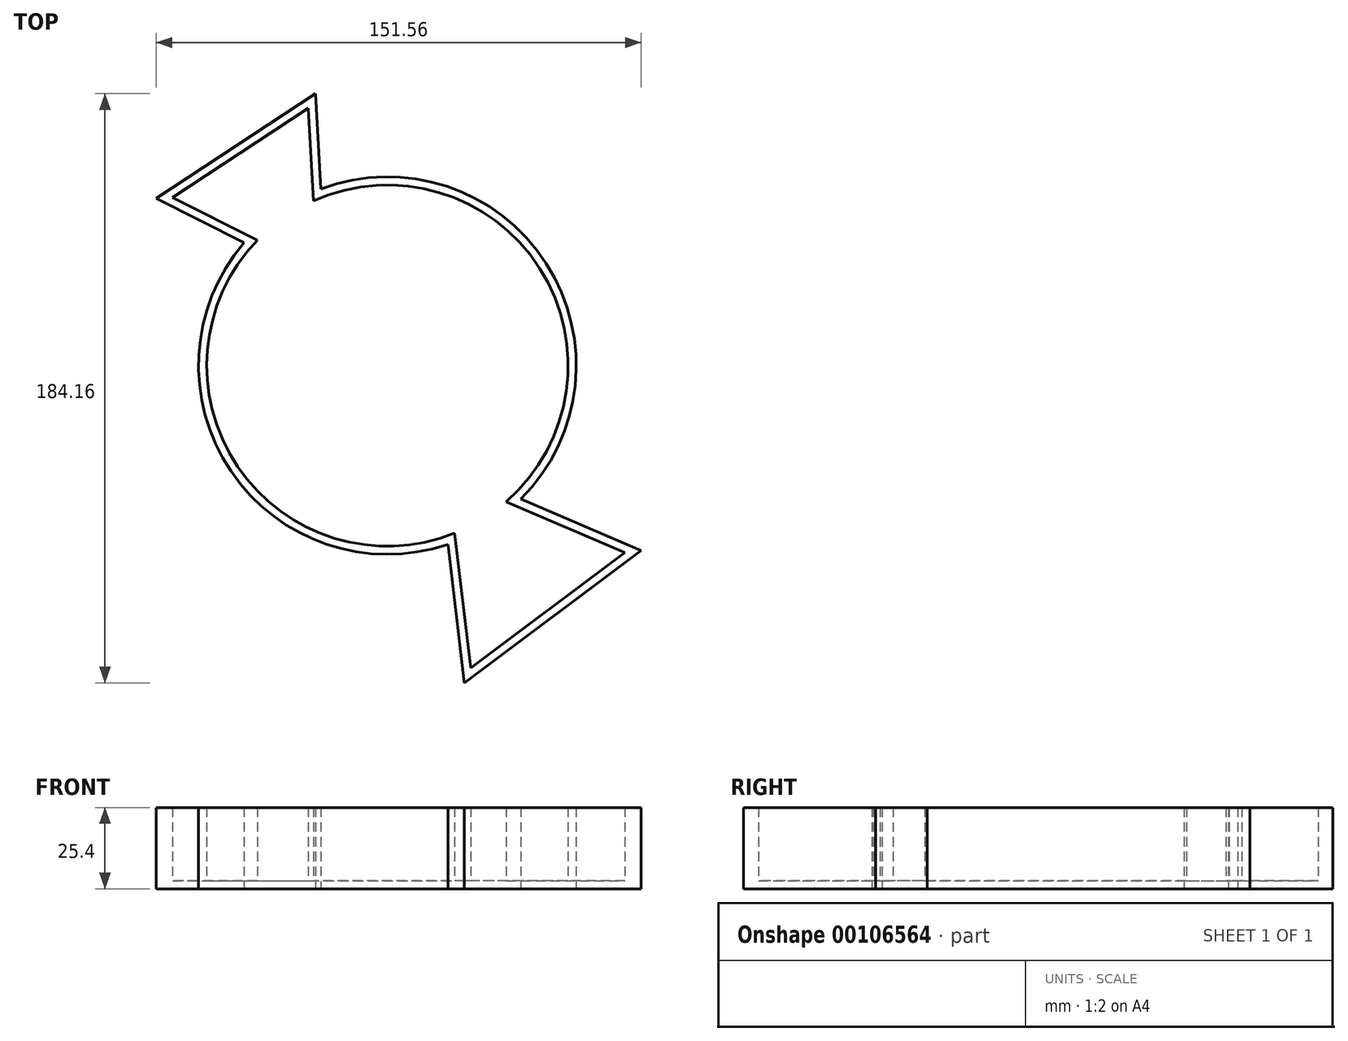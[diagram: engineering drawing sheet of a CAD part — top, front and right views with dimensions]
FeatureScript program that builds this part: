
annotation { "Feature Type Name" : "Feature", "Feature Type Description" : "" }
export const myFeature = defineFeature(function(context is Context, id is Id, definition is map)
    precondition{}
    {
        {
            var Q0;
            Q0=qCreatedBy(makeId("Top.planeOp"),FACE);
            var sketch = newSketch(context, id + "F0", { "sketchPlane" : qUnion([Q0])});
            skCircle(sketch, "E0", {"center": v(0, 0) * mm, "radius": 59 * mm});
            skCircle(sketch, "E1.cCircle", {"center": v(-37.93, 54.25) * mm, "radius": 17.2 * mm, "construction": true});
            skLineSegment(sketch, "E1.0", {"start": v(-22.47, 84.98) * mm, "end": v(-19.05, 25.49) * mm});
            skLineSegment(sketch, "E1.1", {"start": v(-19.05, 25.49) * mm, "end": v(-72.27, 52.27) * mm});
            skLineSegment(sketch, "E1.2", {"start": v(-72.27, 52.27) * mm, "end": v(-22.47, 84.98) * mm});
            skPoint(sketch, "E1.0.midPoint", {"position": v(-20.76, 55.23) * mm});
            skCircle(sketch, "E2.cCircle", {"center": v(39.74, -62.58) * mm, "radius": 19.92 * mm, "construction": true});
            skLineSegment(sketch, "E2.0", {"start": v(79.3, -57.9) * mm, "end": v(24.02, -99.18) * mm});
            skLineSegment(sketch, "E2.1", {"start": v(24.02, -99.18) * mm, "end": v(15.9, -30.67) * mm});
            skLineSegment(sketch, "E2.2", {"start": v(15.9, -30.67) * mm, "end": v(79.3, -57.9) * mm});
            skPoint(sketch, "E2.0.midPoint", {"position": v(51.65, -78.54) * mm});
            skSolve(sketch);
        }
        {
            var Q0;
            {var subQ5=sQuery(id+"F0.wireOp",EDGE,"E1.2");Q0=makeQuery(id+"F0.imprint","IMPRINT",FACE,{"disambiguationData":[TD([[makeQuery(id+"F0.imprint","IMPRINT",EDGE,{"derivedFrom":subQ5}),-1.0]])]});}
            var Q1;
            {var subQ0=sQuery(id+"F0.wireOp",EDGE,"E1.1");var subQ1=sQuery(id+"F0.wireOp",EDGE,"E0");var subQ2=makeQuery(id+"F0.imprint","INTERSECT",VERTEX,{"derivedFrom":[subQ1,subQ0]});Q1=makeQuery(id+"F0.imprint","IMPRINT",FACE,{"disambiguationData":[TD([[makeQuery(id+"F0.imprint","IMPRINT",EDGE,{"disambiguationData":[TD([[subQ2,1.0]])],"derivedFrom":subQ1}),1.0]])]});}
            var Q2;
            {var subQ0=sQuery(id+"F0.wireOp",EDGE,"E1.1");var subQ3=sQuery(id+"F0.wireOp",EDGE,"E0");var subQ4=makeQuery(id+"F0.imprint","INTERSECT",VERTEX,{"derivedFrom":[subQ3,subQ0]});Q2=makeQuery(id+"F0.imprint","IMPRINT",FACE,{"disambiguationData":[TD([[makeQuery(id+"F0.imprint","IMPRINT",EDGE,{"disambiguationData":[TD([[subQ4,-1.0]])],"derivedFrom":subQ3}),1.0]])]});}
            var Q3;
            {var subQ5=sQuery(id+"F0.wireOp",EDGE,"E2.0");Q3=makeQuery(id+"F0.imprint","IMPRINT",FACE,{"disambiguationData":[TD([[makeQuery(id+"F0.imprint","IMPRINT",EDGE,{"derivedFrom":subQ5}),-1.0]])]});}
            var Q4;
            {var subQ0=sQuery(id+"F0.wireOp",EDGE,"E2.1");var subQ1=sQuery(id+"F0.wireOp",EDGE,"E0");var subQ2=makeQuery(id+"F0.imprint","INTERSECT",VERTEX,{"derivedFrom":[subQ1,subQ0]});Q4=makeQuery(id+"F0.imprint","IMPRINT",FACE,{"disambiguationData":[TD([[makeQuery(id+"F0.imprint","IMPRINT",EDGE,{"disambiguationData":[TD([[subQ2,-1.0]])],"derivedFrom":subQ1}),1.0]])]});}
            extrude(context, id + "F1", {"entities" : qUnion([Q0, Q1, Q2, Q3, Q4]), "depth" : 25.4 * mm});
        }
        {
            var Q0;
            Q0=makeQuery(id+"F1.opExtrude","CAP_FACE",FACE,{"disambiguationData":[OSD([sQuery(id+"F0.wireOp",EDGE,"E0"),sQuery(id+"F0.wireOp",EDGE,"E1.0"),sQuery(id+"F0.wireOp",EDGE,"E1.1"),sQuery(id+"F0.wireOp",EDGE,"E1.2"),sQuery(id+"F0.wireOp",EDGE,"E2.0"),sQuery(id+"F0.wireOp",EDGE,"E2.1"),sQuery(id+"F0.wireOp",EDGE,"E2.2")])],"isStart":false});
            shell(context, id + "F2", {"entities" : qUnion([Q0]), "thickness" : 2.54 * mm});
        }
    });
